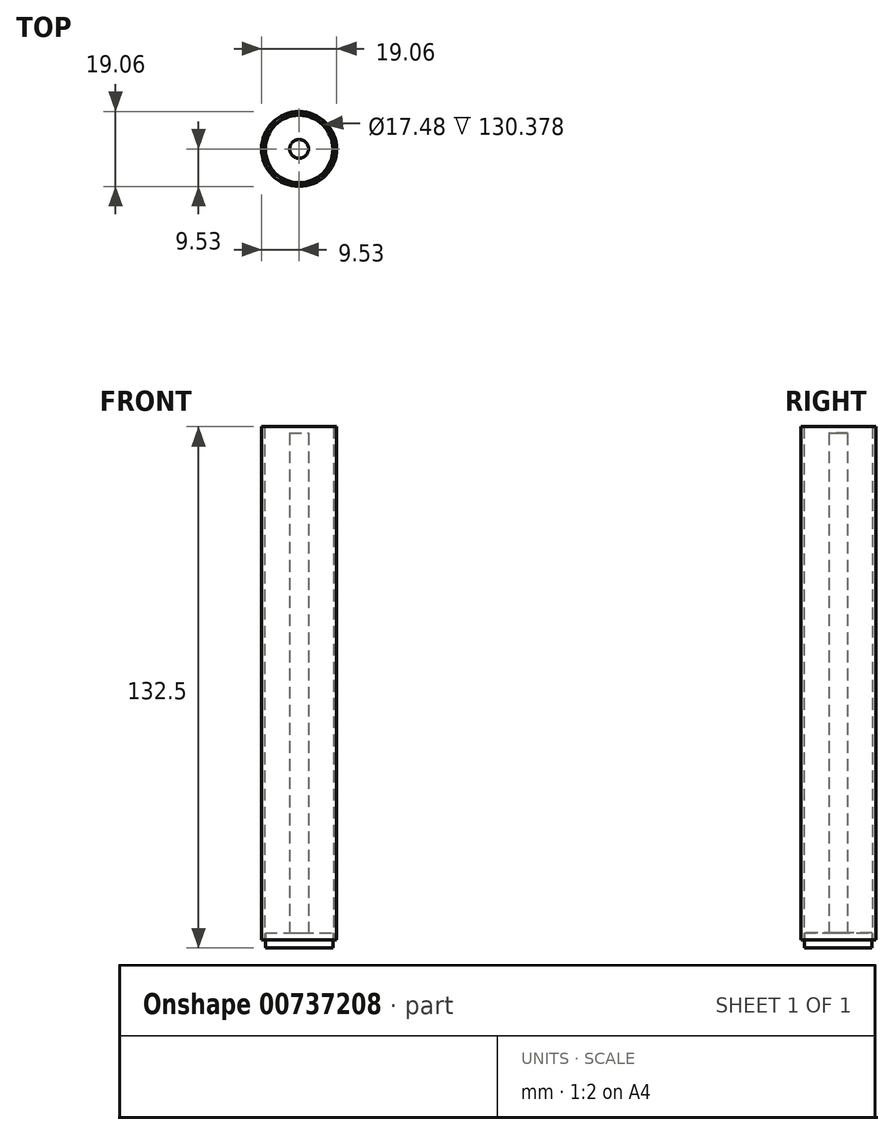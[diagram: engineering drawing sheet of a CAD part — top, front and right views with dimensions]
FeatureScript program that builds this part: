
annotation { "Feature Type Name" : "Feature", "Feature Type Description" : "" }
export const myFeature = defineFeature(function(context is Context, id is Id, definition is map)
    precondition{}
    {
        {
            var Q0;
            Q0=qCreatedBy(makeId("Top.planeOp"),FACE);
            var sketch = newSketch(context, id + "F0", { "sketchPlane" : qUnion([Q0])});
            skCircle(sketch, "E0", {"center": v(0, 0) * mm, "radius": 9.53 * mm});
            skCircle(sketch, "E1", {"center": v(0, 0) * mm, "radius": 8.74 * mm});
            skSolve(sketch);
        }
        {
            var Q0;
            Q0=makeQuery(id+"F0.imprint","IMPRINT",FACE,{"disambiguationData":[TD([[makeQuery(id+"F0.imprint","IMPRINT",EDGE,{"derivedFrom":sQuery(id+"F0.wireOp",EDGE,"E0")}),1.0]])]});
            extrude(context, id + "F1", {"entities" : qUnion([Q0]), "endBound" : BoundingType.SYMMETRIC, "depth" : 130.38 * mm, "offsetDistance" : 25.4 * mm});
        }
        {
            var Q0;
            Q0=qCreatedBy(makeId("Front.planeOp"),FACE);
            var sketch = newSketch(context, id + "F2", { "sketchPlane" : qUnion([Q0])});
            skLineSegment(sketch, "E2.top", {"start": v(-8.9, -67.3) * mm, "end": v(8.57, -67.3) * mm});
            skLineSegment(sketch, "E2.left", {"start": v(-8.9, -63.5) * mm, "end": v(-8.9, -67.31) * mm});
            skLineSegment(sketch, "E2.right", {"start": v(8.57, -63.5) * mm, "end": v(8.57, -67.3) * mm});
            skLineSegment(sketch, "E3.top", {"start": v(2.39, 63.5) * mm, "end": v(-2.39, 63.5) * mm});
            skLineSegment(sketch, "E3.left", {"start": v(2.39, -63.5) * mm, "end": v(2.39, 63.5) * mm});
            skLineSegment(sketch, "E3.right", {"start": v(-2.39, -63.5) * mm, "end": v(-2.39, 63.5) * mm});
            skPoint(sketch, "E3.middle", {"position": v(0, 0) * mm});
            skLineSegment(sketch, "E4", {"start": v(2.39, -63.5) * mm, "end": v(8.57, -63.5) * mm});
            skLineSegment(sketch, "E5", {"start": v(-2.39, -63.5) * mm, "end": v(-8.9, -63.5) * mm});
            skLineSegment(sketch, "E6", {"start": v(0, -67.3) * mm, "end": v(0, 63.5) * mm});
            skSolve(sketch);
        }
        {
            var Q0;
            {var subQ3=sQuery(id+"F2.wireOp",EDGE,"E2.right");Q0=makeQuery(id+"F2.imprint","IMPRINT",FACE,{"disambiguationData":[TD([[makeQuery(id+"F2.imprint","IMPRINT",EDGE,{"derivedFrom":subQ3}),-1.0]])]});}
            var Q1;
            Q1=sQuery(id+"F2.wireOp",EDGE,"E6");
            revolve(context, id + "F3", {"surfaceOperationType" : NewSurfaceOperationType.NEW, "entities" : qUnion([Q0]), "axis" : qUnion([Q1]), "revolveType" : RevolveType.FULL});
        }
    });
